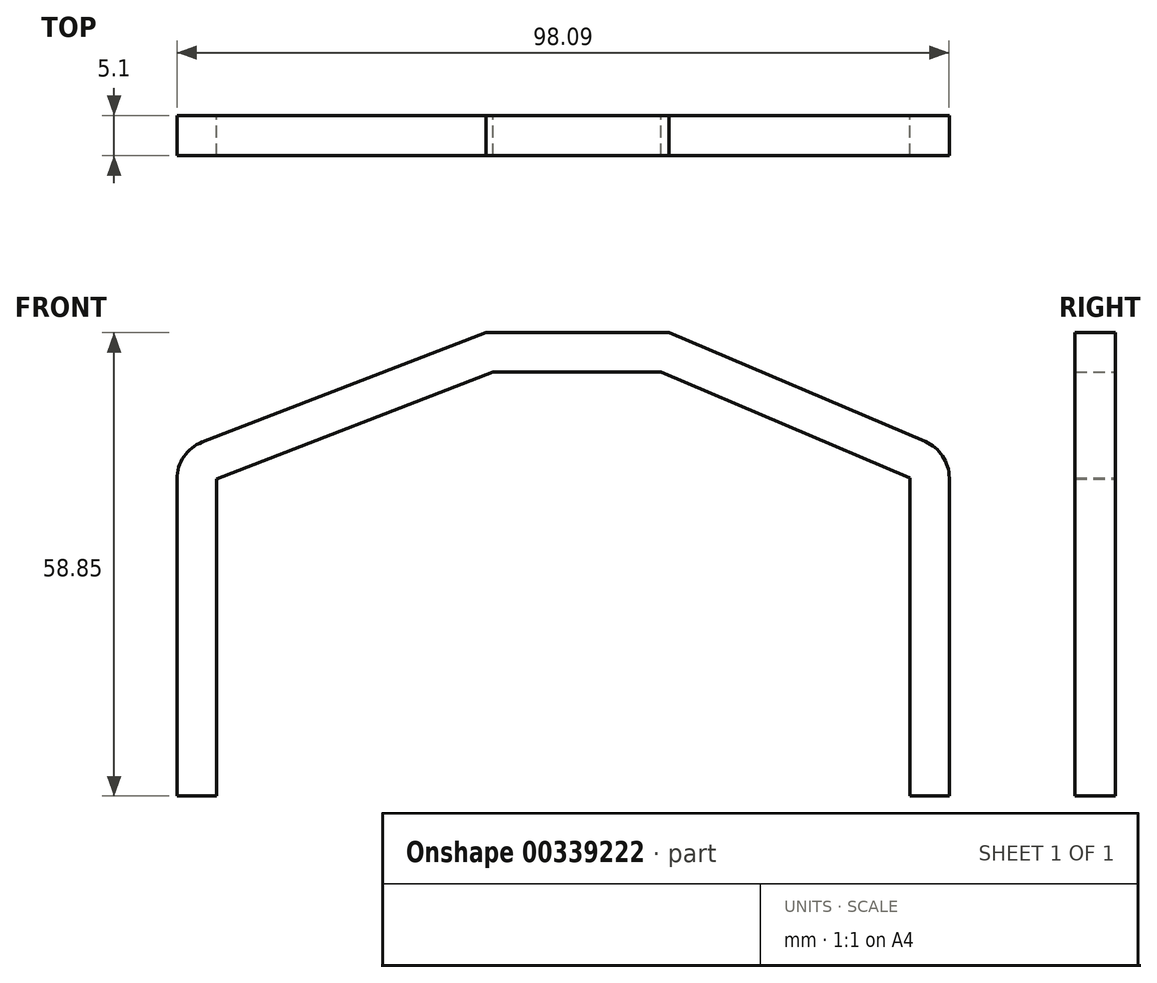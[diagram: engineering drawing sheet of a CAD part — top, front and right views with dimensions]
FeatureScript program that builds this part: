
annotation { "Feature Type Name" : "Feature", "Feature Type Description" : "" }
export const myFeature = defineFeature(function(context is Context, id is Id, definition is map)
    precondition{}
    {
        {
            var Q0;
            Q0=qCreatedBy(makeId("Front.planeOp"),FACE);
            var sketch = newSketch(context, id + "F0", { "sketchPlane" : qUnion([Q0])});
            skLineSegment(sketch, "E0", {"start": v(-50.73, 0) * mm, "end": v(-50.73, 40.29) * mm});
            skLineSegment(sketch, "E1", {"start": v(-47.52, 44.95) * mm, "end": v(-11.5, 58.85) * mm});
            skLineSegment(sketch, "E2", {"start": v(-11.5, 58.85) * mm, "end": v(11.77, 58.85) * mm});
            skLineSegment(sketch, "E3", {"start": v(11.77, 58.85) * mm, "end": v(44.32, 45.01) * mm});
            skLineSegment(sketch, "E4", {"start": v(47.36, 40.41) * mm, "end": v(47.36, 0) * mm});
            skLineSegment(sketch, "E5.0", {"start": v(42.36, 40.41) * mm, "end": v(42.36, 0) * mm});
            skLineSegment(sketch, "E5.1", {"start": v(-45.73, 0) * mm, "end": v(-45.73, 40.29) * mm});
            skLineSegment(sketch, "E5.2", {"start": v(-45.73, 40.29) * mm, "end": v(-10.56, 53.85) * mm});
            skLineSegment(sketch, "E5.3", {"start": v(-10.56, 53.85) * mm, "end": v(10.75, 53.85) * mm});
            skLineSegment(sketch, "E5.4", {"start": v(10.75, 53.85) * mm, "end": v(42.36, 40.41) * mm});
            skPoint(sketch, "E6.visualSharp", {"position": v(-50.73, 43.72) * mm});
            skArc(sketch, "E6.filletArc", {"start": v(-47.52, 44.95) * mm, "mid": v(-49.85, 43.12) * mm, "end": v(-50.73, 40.29) * mm});
            skPoint(sketch, "E7.visualSharp", {"position": v(47.36, 43.72) * mm});
            skArc(sketch, "E7.filletArc", {"start": v(47.36, 40.41) * mm, "mid": v(46.53, 43.17) * mm, "end": v(44.32, 45.01) * mm});
            skLineSegment(sketch, "E8", {"start": v(-50.73, 0) * mm, "end": v(-45.73, 0) * mm});
            skLineSegment(sketch, "E9", {"start": v(42.36, 0) * mm, "end": v(47.36, 0) * mm});
            skSolve(sketch);
        }
        {
            var Q0;
            Q0=makeQuery(id+"F0.imprint","IMPRINT",FACE,{"disambiguationData":[TD([[makeQuery(id+"F0.imprint","IMPRINT",EDGE,{"derivedFrom":sQuery(id+"F0.wireOp",EDGE,"E0")}),-1.0]])]});
            extrude(context, id + "F1", {"entities" : qUnion([Q0]), "depth" : 5.1 * mm});
        }
        {
            var Q0;
            Q0=makeQuery(id+"F1.opExtrude","SWEPT_BODY",BODY,{"disambiguationData":[OSD([sQuery(id+"F0.wireOp",EDGE,"E0"),sQuery(id+"F0.wireOp",EDGE,"E1"),sQuery(id+"F0.wireOp",EDGE,"E2"),sQuery(id+"F0.wireOp",EDGE,"E3"),sQuery(id+"F0.wireOp",EDGE,"E4"),sQuery(id+"F0.wireOp",EDGE,"E5.0"),sQuery(id+"F0.wireOp",EDGE,"E5.1"),sQuery(id+"F0.wireOp",EDGE,"E5.2"),sQuery(id+"F0.wireOp",EDGE,"E5.3"),sQuery(id+"F0.wireOp",EDGE,"E5.4"),sQuery(id+"F0.wireOp",EDGE,"E6.filletArc"),sQuery(id+"F0.wireOp",EDGE,"E7.filletArc"),sQuery(id+"F0.wireOp",EDGE,"E8"),sQuery(id+"F0.wireOp",EDGE,"E9")])]});
            transform(context, id + "F2", {"entities" : qUnion([Q0]), "transformType" : TransformType.TRANSLATION_3D, "dx" : 0 * mm, "dy" : 0 * mm, "dz" : 0 * mm, "makeCopy" : true});
        }
    });
